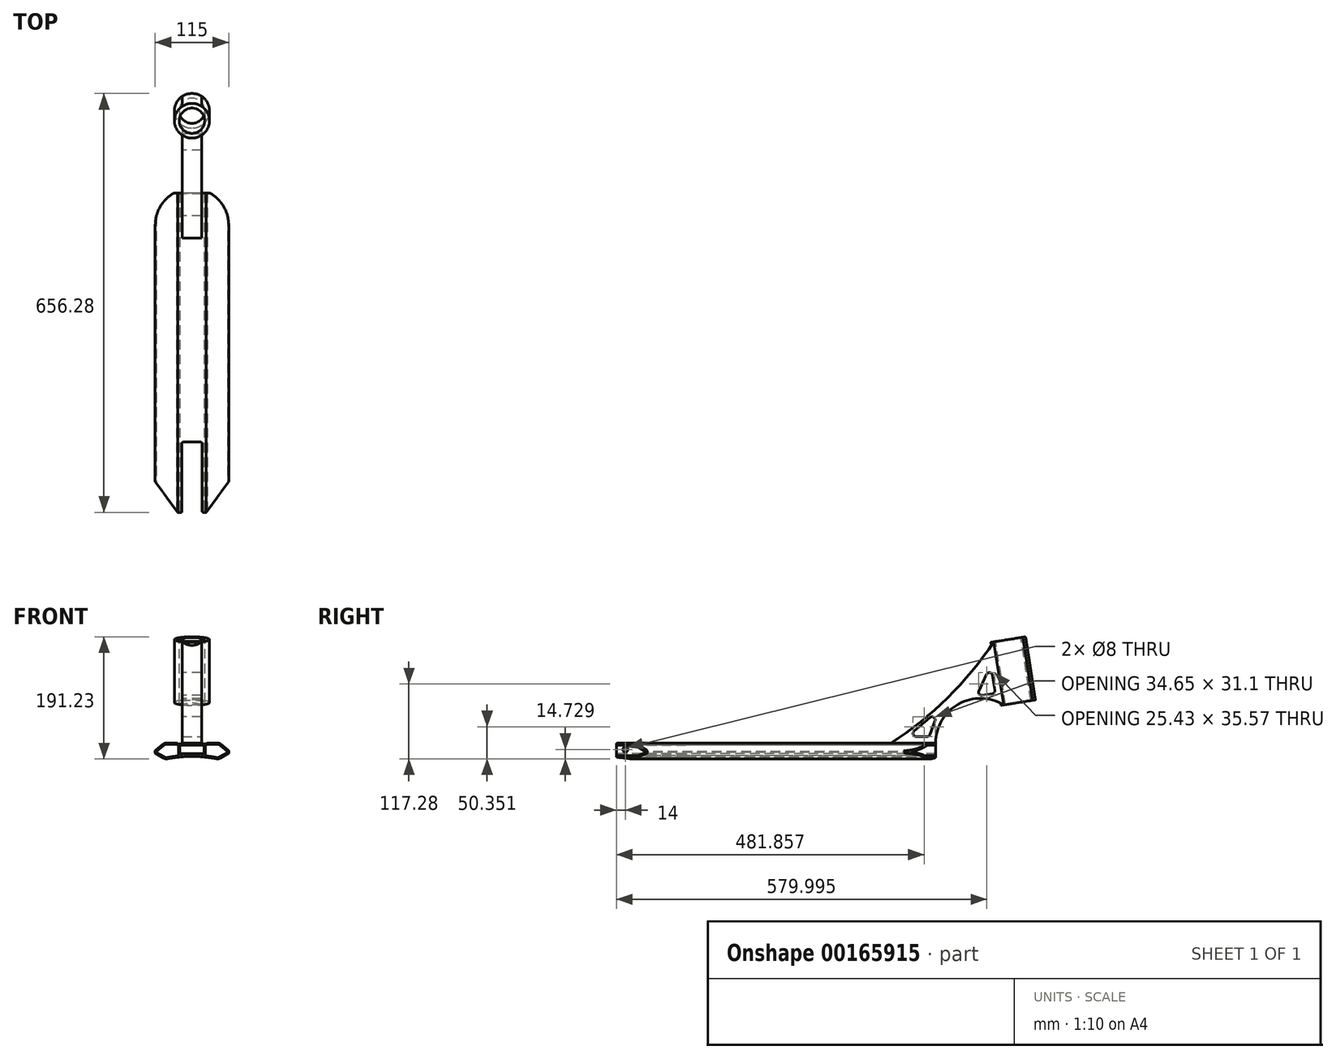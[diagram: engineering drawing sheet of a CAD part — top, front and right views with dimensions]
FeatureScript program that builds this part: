
annotation { "Feature Type Name" : "Feature", "Feature Type Description" : "" }
export const myFeature = defineFeature(function(context is Context, id is Id, definition is map)
    precondition{}
    {
        {
            var Q0;
            Q0=qCreatedBy(makeId("Front.planeOp"),FACE);
            var sketch = newSketch(context, id + "F0", { "sketchPlane" : qUnion([Q0])});
            skLineSegment(sketch, "E0", {"start": v(0, 45.15) * mm, "end": v(0, 0) * mm, "construction": true});
            skLineSegment(sketch, "E1", {"start": v(0, 10.68) * mm, "end": v(22.5, 10.68) * mm});
            skLineSegment(sketch, "E2", {"start": v(22.5, 10.68) * mm, "end": v(22.5, 11.98) * mm});
            skLineSegment(sketch, "E3", {"start": v(22.5, 11.98) * mm, "end": v(43.22, 11.98) * mm});
            skLineSegment(sketch, "E4", {"start": v(43.22, 11.98) * mm, "end": v(57.5, 0) * mm});
            skLineSegment(sketch, "E5", {"start": v(57.5, 0) * mm, "end": v(57.5, -4) * mm});
            skLineSegment(sketch, "E6", {"start": v(57.5, -4) * mm, "end": v(41.36, -13.32) * mm});
            skLineSegment(sketch, "E7.MirrorCS", {"start": v(0, 10.68) * mm, "end": v(-22.5, 10.68) * mm});
            skLineSegment(sketch, "E8.MirrorCS", {"start": v(-22.5, 10.68) * mm, "end": v(-22.5, 11.98) * mm});
            skLineSegment(sketch, "E9.MirrorCS", {"start": v(-22.5, 11.98) * mm, "end": v(-43.22, 11.98) * mm});
            skLineSegment(sketch, "E10.MirrorCS", {"start": v(-43.22, 11.98) * mm, "end": v(-57.5, 0) * mm});
            skLineSegment(sketch, "E11.MirrorCS", {"start": v(-57.5, 0) * mm, "end": v(-57.5, -4) * mm});
            skLineSegment(sketch, "E12.MirrorCS", {"start": v(-57.5, -4) * mm, "end": v(-41.36, -13.32) * mm});
            skArc(sketch, "E13", {"start": v(41.36, -13.32) * mm, "mid": v(0, -9) * mm, "end": v(-41.36, -13.32) * mm});
            skSolve(sketch);
        }
        {
            var Q0;
            Q0 = qSketchRegion(id + "F0", true);
            extrude(context, id + "F1", {"entities" : qUnion([Q0]), "endBound" : BoundingType.SYMMETRIC, "depth" : 500 * mm});
        }
        {
            var Q0;
            Q0=makeQuery(id+"F1.opExtrude","CAP_FACE",FACE,{"disambiguationData":[OSD([sQuery(id+"F0.wireOp",EDGE,"E1"),sQuery(id+"F0.wireOp",EDGE,"E2"),sQuery(id+"F0.wireOp",EDGE,"E3"),sQuery(id+"F0.wireOp",EDGE,"E4"),sQuery(id+"F0.wireOp",EDGE,"E5"),sQuery(id+"F0.wireOp",EDGE,"E6"),sQuery(id+"F0.wireOp",EDGE,"E7.MirrorCS"),sQuery(id+"F0.wireOp",EDGE,"E8.MirrorCS"),sQuery(id+"F0.wireOp",EDGE,"E9.MirrorCS"),sQuery(id+"F0.wireOp",EDGE,"E10.MirrorCS"),sQuery(id+"F0.wireOp",EDGE,"E11.MirrorCS"),sQuery(id+"F0.wireOp",EDGE,"E12.MirrorCS"),sQuery(id+"F0.wireOp",EDGE,"E13")])],"isStart":false});
            var sketch = newSketch(context, id + "F2", { "sketchPlane" : qUnion([Q0])});
            skPoint(sketch, "E14.firstSnap0", {"position": v(-50.36, 8.68) * mm});
            skLineSegment(sketch, "E14.top", {"start": v(-19, -4.32) * mm, "end": v(19, -4.32) * mm});
            skLineSegment(sketch, "E14.left", {"start": v(-19, 8.68) * mm, "end": v(-19, -4.32) * mm});
            skLineSegment(sketch, "E14.right", {"start": v(19, 8.68) * mm, "end": v(19, -4.32) * mm});
            skLineSegment(sketch, "E15", {"start": v(-19, 8.68) * mm, "end": v(19, 8.68) * mm});
            skSolve(sketch);
        }
        {
            var Q0;
            Q0 = qSketchRegion(id + "F2", true);
            extrude(context, id + "F3", {"entities" : qUnion([Q0]), "operationType" : NewBodyOperationType.REMOVE, "endBound" : BoundingType.THROUGH_ALL, "oppositeDirection" : true, "depth" : 500 * mm});
        }
        {
            var Q0;
            Q0=makeQuery(id+"F1.opExtrude","SWEPT_EDGE",EDGE,{"disambiguationData":[OSD([sQuery(id+"F0.wireOp",EDGE,"E8.MirrorCS"),sQuery(id+"F0.wireOp",EDGE,"E9.MirrorCS")])]});
            var Q1;
            Q1=makeQuery(id+"F1.opExtrude","SWEPT_EDGE",EDGE,{"disambiguationData":[OSD([sQuery(id+"F0.wireOp",EDGE,"E2"),sQuery(id+"F0.wireOp",EDGE,"E3")])]});
            fillet(context, id + "F4", {"entities" : qUnion([Q0, Q1]), "radius" : 2 * mm, "tangentPropagation" : true, "allowEdgeOverflow" : false});
        }
        {
            var Q0;
            Q0=makeQuery(id+"F1.opExtrude","SWEPT_EDGE",EDGE,{"disambiguationData":[OSD([sQuery(id+"F0.wireOp",EDGE,"E12.MirrorCS"),sQuery(id+"F0.wireOp",EDGE,"E13")])]});
            var Q1;
            Q1=makeQuery(id+"F1.opExtrude","SWEPT_EDGE",EDGE,{"disambiguationData":[OSD([sQuery(id+"F0.wireOp",EDGE,"E6"),sQuery(id+"F0.wireOp",EDGE,"E13")])]});
            var Q2;
            Q2=makeQuery(id+"F1.opExtrude","SWEPT_EDGE",EDGE,{"disambiguationData":[OSD([sQuery(id+"F0.wireOp",EDGE,"E9.MirrorCS"),sQuery(id+"F0.wireOp",EDGE,"E10.MirrorCS")])]});
            var Q3;
            Q3=makeQuery(id+"F1.opExtrude","SWEPT_EDGE",EDGE,{"disambiguationData":[OSD([sQuery(id+"F0.wireOp",EDGE,"E3"),sQuery(id+"F0.wireOp",EDGE,"E4")])]});
            fillet(context, id + "F5", {"entities" : qUnion([Q0, Q1, Q2, Q3]), "radius" : 9 * mm, "tangentPropagation" : true, "allowEdgeOverflow" : false});
        }
        {
            var Q0;
            Q0=makeQuery(id+"F1.opExtrude","SWEPT_EDGE",EDGE,{"disambiguationData":[OSD([sQuery(id+"F0.wireOp",EDGE,"E4"),sQuery(id+"F0.wireOp",EDGE,"E5")])]});
            var Q1;
            Q1=makeQuery(id+"F1.opExtrude","SWEPT_EDGE",EDGE,{"disambiguationData":[OSD([sQuery(id+"F0.wireOp",EDGE,"E5"),sQuery(id+"F0.wireOp",EDGE,"E6")])]});
            var Q2;
            Q2=makeQuery(id+"F1.opExtrude","SWEPT_EDGE",EDGE,{"disambiguationData":[OSD([sQuery(id+"F0.wireOp",EDGE,"E10.MirrorCS"),sQuery(id+"F0.wireOp",EDGE,"E11.MirrorCS")])]});
            var Q3;
            Q3=makeQuery(id+"F1.opExtrude","SWEPT_EDGE",EDGE,{"disambiguationData":[OSD([sQuery(id+"F0.wireOp",EDGE,"E11.MirrorCS"),sQuery(id+"F0.wireOp",EDGE,"E12.MirrorCS")])]});
            fillet(context, id + "F6", {"entities" : qUnion([Q0, Q1, Q2, Q3]), "radius" : 1 * mm, "tangentPropagation" : true, "allowEdgeOverflow" : false});
        }
        {
            var Q0;
            Q0=makeQuery(id+"F1.opExtrude","CAP_FACE",FACE,{"disambiguationData":[OSD([sQuery(id+"F0.wireOp",EDGE,"E1"),sQuery(id+"F0.wireOp",EDGE,"E2"),sQuery(id+"F0.wireOp",EDGE,"E3"),sQuery(id+"F0.wireOp",EDGE,"E4"),sQuery(id+"F0.wireOp",EDGE,"E5"),sQuery(id+"F0.wireOp",EDGE,"E6"),sQuery(id+"F0.wireOp",EDGE,"E7.MirrorCS"),sQuery(id+"F0.wireOp",EDGE,"E8.MirrorCS"),sQuery(id+"F0.wireOp",EDGE,"E9.MirrorCS"),sQuery(id+"F0.wireOp",EDGE,"E10.MirrorCS"),sQuery(id+"F0.wireOp",EDGE,"E11.MirrorCS"),sQuery(id+"F0.wireOp",EDGE,"E12.MirrorCS"),sQuery(id+"F0.wireOp",EDGE,"E13")])],"isStart":false});
            var sketch = newSketch(context, id + "F7", { "sketchPlane" : qUnion([Q0])});
            skLineSegment(sketch, "E16.0", {"start": v(-22.5, 10.68) * mm, "end": v(-21, 10.68) * mm});
            skPoint(sketch, "E17.0", {"position": v(-23.23, 11.62) * mm});
            skLineSegment(sketch, "E18.0", {"start": v(-24.37, 11.98) * mm, "end": v(-39.95, 11.98) * mm});
            skArc(sketch, "E19.0", {"start": v(-39.95, 11.98) * mm, "mid": v(-43.02, 11.44) * mm, "end": v(-45.73, 9.88) * mm});
            skLineSegment(sketch, "E20.0", {"start": v(-45.73, 9.88) * mm, "end": v(-57.14, 0.3) * mm});
            skPoint(sketch, "E21.0", {"position": v(-57.4, -0.04) * mm});
            skPoint(sketch, "E22.0", {"position": v(-57.5, -1.94) * mm});
            skPoint(sketch, "E23.0", {"position": v(-57, -4.29) * mm});
            skLineSegment(sketch, "E24.0", {"start": v(-57, -4.29) * mm, "end": v(-44.3, -11.62) * mm});
            skArc(sketch, "E25.0", {"start": v(-44.3, -11.62) * mm, "mid": v(-41.3, -12.7) * mm, "end": v(-38.1, -12.66) * mm});
            skArc(sketch, "E26.0", {"start": v(-21, -10.1) * mm, "mid": v(-29.57, -11.2) * mm, "end": v(-38.1, -12.66) * mm});
            skLineSegment(sketch, "E27", {"start": v(-21, 8.68) * mm, "end": v(-21, -8.1) * mm});
            skLineSegment(sketch, "E28.0", {"start": v(-44.45, 8.34) * mm, "end": v(-55.86, -1.23) * mm});
            skArc(sketch, "E28.1", {"start": v(-39.95, 9.98) * mm, "mid": v(-42.34, 9.56) * mm, "end": v(-44.45, 8.34) * mm});
            skLineSegment(sketch, "E29.0", {"start": v(-24.37, 9.98) * mm, "end": v(-39.95, 9.98) * mm});
            skLineSegment(sketch, "E30.0", {"start": v(-22.5, 8.68) * mm, "end": v(-21, 8.68) * mm});
            skFitSpline(sketch, "E31", {"points": [v(-24.37, 9.98) * mm, v(-22.5, 8.68) * mm], "startDerivative": vector(1.87, -1.3) * mm, "endDerivative": vector(1.87, -1.3) * mm});
            skFitSpline(sketch, "E32", {"points": [v(-23.12, 9.11) * mm, v(-23.48, 9.36) * mm], "startDerivative": vector(-0.35, 0.24) * mm, "endDerivative": vector(-0.35, 0.24) * mm});
            skLineSegment(sketch, "E33.0", {"start": v(-56, -2.56) * mm, "end": v(-43.3, -9.88) * mm});
            skArc(sketch, "E33.1", {"start": v(-43.3, -9.88) * mm, "mid": v(-40.96, -10.73) * mm, "end": v(-38.47, -10.7) * mm});
            skArc(sketch, "E33.2", {"start": v(-21, -8.1) * mm, "mid": v(-29.77, -9.2) * mm, "end": v(-38.47, -10.7) * mm});
            skLineSegment(sketch, "E34", {"start": v(-55.86, -1.23) * mm, "end": v(-56, -2.56) * mm});
            skLineSegment(sketch, "E35.MirrorCS", {"start": v(21, 8.68) * mm, "end": v(21, -8.1) * mm});
            skArc(sketch, "E36.MirrorCS", {"start": v(21, -8.1) * mm, "mid": v(29.77, -9.2) * mm, "end": v(38.47, -10.7) * mm});
            skArc(sketch, "E37.MirrorCS", {"start": v(43.3, -9.88) * mm, "mid": v(40.96, -10.73) * mm, "end": v(38.47, -10.7) * mm});
            skLineSegment(sketch, "E38.MirrorCS", {"start": v(56, -2.56) * mm, "end": v(43.3, -9.88) * mm});
            skLineSegment(sketch, "E39.MirrorCS", {"start": v(55.86, -1.23) * mm, "end": v(56, -2.56) * mm});
            skLineSegment(sketch, "E40.MirrorCS", {"start": v(44.45, 8.34) * mm, "end": v(55.86, -1.23) * mm});
            skArc(sketch, "E41.MirrorCS", {"start": v(39.95, 9.98) * mm, "mid": v(42.34, 9.56) * mm, "end": v(44.45, 8.34) * mm});
            skLineSegment(sketch, "E42.MirrorCS", {"start": v(24.37, 9.98) * mm, "end": v(39.95, 9.98) * mm});
            skLineSegment(sketch, "E43.MirrorCS", {"start": v(22.5, 8.68) * mm, "end": v(21, 8.68) * mm});
            skLineSegment(sketch, "E44", {"start": v(24.37, 9.98) * mm, "end": v(22.5, 8.68) * mm});
            skSolve(sketch);
        }
        {
            var Q0;
            Q0 = qSketchRegion(id + "F7", true);
            extrude(context, id + "F8", {"entities" : qUnion([Q0]), "operationType" : NewBodyOperationType.REMOVE, "endBound" : BoundingType.THROUGH_ALL, "oppositeDirection" : true, "depth" : 25 * mm});
        }
        {
            var Q0;
            Q0 = qSketchRegion(id + "F7", true);
            extrude(context, id + "F9", {"entities" : qUnion([Q0]), "operationType" : NewBodyOperationType.REMOVE, "endBound" : BoundingType.THROUGH_ALL, "oppositeDirection" : true, "depth" : 25 * mm});
        }
        {
            var Q0;
            Q0=makeQuery(id+"F1.opExtrude","SWEPT_FACE",FACE,{"disambiguationData":[OSD([sQuery(id+"F0.wireOp",EDGE,"E1"),sQuery(id+"F0.wireOp",EDGE,"E7.MirrorCS")])]});
            var sketch = newSketch(context, id + "F10", { "sketchPlane" : qUnion([Q0])});
            skArc(sketch, "E45", {"start": v(57.5, 200) * mm, "mid": v(0, 257.5) * mm, "end": v(-57.5, 200) * mm});
            skLineSegment(sketch, "E46", {"start": v(-57.5, 280) * mm, "end": v(57.5, 280) * mm});
            skLineSegment(sketch, "E47", {"start": v(57.5, 200) * mm, "end": v(57.5, 280) * mm});
            skPoint(sketch, "E48.orphan", {"position": v(63.8, 280) * mm});
            skLineSegment(sketch, "E49", {"start": v(-57.5, 200) * mm, "end": v(-57.5, 280) * mm});
            skPoint(sketch, "E50.orphan", {"position": v(-57.5, 278.01) * mm});
            skSolve(sketch);
        }
        {
            var Q0;
            Q0 = qSketchRegion(id + "F10", true);
            extrude(context, id + "F11", {"entities" : qUnion([Q0]), "operationType" : NewBodyOperationType.REMOVE, "endBound" : BoundingType.SYMMETRIC, "oppositeDirection" : true, "depth" : 100 * mm});
        }
        {
            var Q0;
            Q0=makeQuery(id+"F1.opExtrude","SWEPT_FACE",FACE,{"disambiguationData":[OSD([sQuery(id+"F0.wireOp",EDGE,"E9.MirrorCS")])]});
            var sketch = newSketch(context, id + "F12", { "sketchPlane" : qUnion([Q0])});
            skLineSegment(sketch, "E51", {"start": v(-68, -187.37) * mm, "end": v(-22.5, -250) * mm});
            skLineSegment(sketch, "E52", {"start": v(-22.5, -250) * mm, "end": v(-16, -250) * mm});
            skLineSegment(sketch, "E53", {"start": v(-16, -250) * mm, "end": v(-16, -140) * mm});
            skLineSegment(sketch, "E54", {"start": v(-16, -140) * mm, "end": v(16, -140) * mm});
            skLineSegment(sketch, "E55", {"start": v(16, -140) * mm, "end": v(16, -250) * mm});
            skLineSegment(sketch, "E56", {"start": v(16, -250) * mm, "end": v(22.5, -250) * mm});
            skLineSegment(sketch, "E57", {"start": v(22.5, -250) * mm, "end": v(68, -187.37) * mm});
            skLineSegment(sketch, "E58", {"start": v(68, -187.37) * mm, "end": v(68, -287.37) * mm});
            skLineSegment(sketch, "E59", {"start": v(68, -287.37) * mm, "end": v(-68, -287.37) * mm});
            skLineSegment(sketch, "E60", {"start": v(-68, -287.37) * mm, "end": v(-68, -187.37) * mm});
            skSolve(sketch);
        }
        {
            var Q0;
            Q0 = qSketchRegion(id + "F12", true);
            extrude(context, id + "F13", {"entities" : qUnion([Q0]), "operationType" : NewBodyOperationType.REMOVE, "endBound" : BoundingType.THROUGH_ALL, "oppositeDirection" : true, "depth" : 25 * mm});
        }
        {
            var Q0;
            {var subQ2=sQuery(id+"F12.wireOp",EDGE,"E53");Q0=makeQuery(id+"F13.boolean.opBoolean","COPY",EDGE,{"disambiguationData":[TD([makeQuery(id+"F3.boolean.opBoolean","COPY",FACE,{"derivedFrom":makeQuery(id+"F3.opExtrude","SWEPT_FACE",FACE,{"disambiguationData":[OSD([sQuery(id+"F2.wireOp",EDGE,"E15")])]})})])],"derivedFrom":makeQuery(id+"F13.opExtrude","SWEPT_EDGE",EDGE,{"disambiguationData":[OSD([sQuery(id+"F12.wireOp",EDGE,"E52"),subQ2])]})});}
            var Q1;
            {var subQ0=sQuery(id+"F0.wireOp",EDGE,"E13");var subQ1=sQuery(id+"F12.wireOp",EDGE,"E53");Q1=makeQuery(id+"F13.boolean.opBoolean","COPY",EDGE,{"disambiguationData":[TD([makeQuery(id+"F1.opExtrude","SWEPT_FACE",FACE,{"disambiguationData":[OSD([subQ0])]})])],"derivedFrom":makeQuery(id+"F13.opExtrude","SWEPT_EDGE",EDGE,{"disambiguationData":[OSD([sQuery(id+"F12.wireOp",EDGE,"E52"),subQ1])]})});}
            var Q2;
            {var subQ0=sQuery(id+"F12.wireOp",EDGE,"E54");var subQ1=sQuery(id+"F12.wireOp",EDGE,"E53");Q2=makeQuery(id+"F13.boolean.opBoolean","COPY",EDGE,{"disambiguationData":[TD([makeQuery(id+"F1.opExtrude","SWEPT_FACE",FACE,{"disambiguationData":[OSD([sQuery(id+"F0.wireOp",EDGE,"E13")])]})])],"derivedFrom":makeQuery(id+"F13.opExtrude","SWEPT_EDGE",EDGE,{"disambiguationData":[OSD([subQ1,subQ0])]})});}
            var Q3;
            {var subQ0=sQuery(id+"F12.wireOp",EDGE,"E53");var subQ1=sQuery(id+"F12.wireOp",EDGE,"E54");Q3=makeQuery(id+"F13.boolean.opBoolean","COPY",EDGE,{"disambiguationData":[TD([makeQuery(id+"F3.boolean.opBoolean","COPY",FACE,{"derivedFrom":makeQuery(id+"F3.opExtrude","SWEPT_FACE",FACE,{"disambiguationData":[OSD([sQuery(id+"F2.wireOp",EDGE,"E15")])]})})])],"derivedFrom":makeQuery(id+"F13.opExtrude","SWEPT_EDGE",EDGE,{"disambiguationData":[OSD([subQ0,subQ1])]})});}
            var Q4;
            {var subQ0=sQuery(id+"F0.wireOp",EDGE,"E13");var subQ1=sQuery(id+"F12.wireOp",EDGE,"E55");Q4=makeQuery(id+"F13.boolean.opBoolean","COPY",EDGE,{"disambiguationData":[TD([makeQuery(id+"F1.opExtrude","SWEPT_FACE",FACE,{"disambiguationData":[OSD([subQ0])]})])],"derivedFrom":makeQuery(id+"F13.opExtrude","SWEPT_EDGE",EDGE,{"disambiguationData":[OSD([subQ1,sQuery(id+"F12.wireOp",EDGE,"E56")])]})});}
            var Q5;
            {var subQ2=sQuery(id+"F12.wireOp",EDGE,"E55");Q5=makeQuery(id+"F13.boolean.opBoolean","COPY",EDGE,{"disambiguationData":[TD([makeQuery(id+"F3.boolean.opBoolean","COPY",FACE,{"derivedFrom":makeQuery(id+"F3.opExtrude","SWEPT_FACE",FACE,{"disambiguationData":[OSD([sQuery(id+"F2.wireOp",EDGE,"E15")])]})})])],"derivedFrom":makeQuery(id+"F13.opExtrude","SWEPT_EDGE",EDGE,{"disambiguationData":[OSD([subQ2,sQuery(id+"F12.wireOp",EDGE,"E56")])]})});}
            var Q6;
            {var subQ0=sQuery(id+"F12.wireOp",EDGE,"E54");var subQ1=sQuery(id+"F12.wireOp",EDGE,"E55");Q6=makeQuery(id+"F13.boolean.opBoolean","COPY",EDGE,{"disambiguationData":[TD([makeQuery(id+"F1.opExtrude","SWEPT_FACE",FACE,{"disambiguationData":[OSD([sQuery(id+"F0.wireOp",EDGE,"E13")])]})])],"derivedFrom":makeQuery(id+"F13.opExtrude","SWEPT_EDGE",EDGE,{"disambiguationData":[OSD([subQ0,subQ1])]})});}
            var Q7;
            {var subQ0=sQuery(id+"F12.wireOp",EDGE,"E54");var subQ1=sQuery(id+"F12.wireOp",EDGE,"E55");Q7=makeQuery(id+"F13.boolean.opBoolean","COPY",EDGE,{"disambiguationData":[TD([makeQuery(id+"F3.boolean.opBoolean","COPY",FACE,{"derivedFrom":makeQuery(id+"F3.opExtrude","SWEPT_FACE",FACE,{"disambiguationData":[OSD([sQuery(id+"F2.wireOp",EDGE,"E15")])]})})])],"derivedFrom":makeQuery(id+"F13.opExtrude","SWEPT_EDGE",EDGE,{"disambiguationData":[OSD([subQ0,subQ1])]})});}
            fillet(context, id + "F14", {"entities" : qUnion([Q0, Q1, Q2, Q3, Q4, Q5, Q6, Q7]), "radius" : 2 * mm, "tangentPropagation" : true, "allowEdgeOverflow" : false});
        }
        {
            var Q0;
            Q0=qCreatedBy(makeId("Right.planeOp"),FACE);
            var sketch = newSketch(context, id + "F15", { "sketchPlane" : qUnion([Q0])});
            skLineSegment(sketch, "E61", {"start": v(180, 11.98) * mm, "end": v(250, 11.98) * mm});
            skArc(sketch, "E62", {"start": v(356.44, 71.75) * mm, "mid": v(285.73, 73.02) * mm, "end": v(250, 11.98) * mm});
            skLineSegment(sketch, "E63", {"start": v(356.44, 71.75) * mm, "end": v(401.87, 78.94) * mm});
            skLineSegment(sketch, "E64", {"start": v(401.87, 78.94) * mm, "end": v(386.23, 177.71) * mm});
            skLineSegment(sketch, "E65", {"start": v(386.23, 177.71) * mm, "end": v(340.8, 170.52) * mm});
            skArc(sketch, "E66", {"start": v(180, 11.98) * mm, "mid": v(268.62, 82.9) * mm, "end": v(340.8, 170.52) * mm});
            skSolve(sketch);
        }
        {
            var Q0;
            Q0 = qSketchRegion(id + "F15", true);
            extrude(context, id + "F16", {"entities" : qUnion([Q0]), "operationType" : NewBodyOperationType.ADD, "endBound" : BoundingType.SYMMETRIC, "depth" : 30 * mm});
        }
        {
            var Q0;
            Q0=makeQuery(id+"F16.opExtrude","SWEPT_FACE",FACE,{"disambiguationData":[OSD([sQuery(id+"F15.wireOp",EDGE,"E65")])]});
            var sketch = newSketch(context, id + "F17", { "sketchPlane" : qUnion([Q0])});
            skCircle(sketch, "E67", {"center": v(0, 386.28) * mm, "radius": 27.46 * mm});
            skSolve(sketch);
        }
        {
            var Q0;
            Q0 = qSketchRegion(id + "F17", true);
            var Q1;
            Q1=makeQuery(id+"F16.opExtrude","SWEPT_FACE",FACE,{"disambiguationData":[OSD([sQuery(id+"F15.wireOp",EDGE,"E63")])]});
            var Q2;
            Q2=makeQuery(id+"F16.opExtrude","SWEPT_BODY",BODY,{"disambiguationData":[OSD([sQuery(id+"F15.wireOp",EDGE,"E61"),sQuery(id+"F15.wireOp",EDGE,"E62"),sQuery(id+"F15.wireOp",EDGE,"E63"),sQuery(id+"F15.wireOp",EDGE,"E64"),sQuery(id+"F15.wireOp",EDGE,"E65"),sQuery(id+"F15.wireOp",EDGE,"E66")])]});
            extrude(context, id + "F18", {"entities" : qUnion([Q0]), "operationType" : NewBodyOperationType.ADD, "endBound" : BoundingType.UP_TO_SURFACE, "oppositeDirection" : true, "endBoundEntityFace" : qUnion([Q1]), "endBoundEntityBody" : qUnion([Q2]), "depth" : 25 * mm});
        }
        {
            var Q0;
            Q0=makeQuery(id+"F18.boolean.opBoolean","MERGE",FACE,{"derivedFrom":[makeQuery(id+"F16.opExtrude","SWEPT_FACE",FACE,{"disambiguationData":[OSD([sQuery(id+"F15.wireOp",EDGE,"E65")])]}),makeQuery(id+"F18.opExtrude","CAP_FACE",FACE,{"disambiguationData":[OSD([sQuery(id+"F17.wireOp",EDGE,"E67")])],"isStart":true})]});
            var sketch = newSketch(context, id + "F19", { "sketchPlane" : qUnion([Q0])});
            skPoint(sketch, "E68", {"position": v(0, 386.28) * mm});
            skSolve(sketch);
        }
        {
            var Q0;
            Q0=sQuery(id+"F19.wireOp",VERTEX,"E68");
            var Q1;
            Q1=makeQuery(id+"F16.opExtrude","SWEPT_BODY",BODY,{"disambiguationData":[OSD([sQuery(id+"F15.wireOp",EDGE,"E61"),sQuery(id+"F15.wireOp",EDGE,"E62"),sQuery(id+"F15.wireOp",EDGE,"E63"),sQuery(id+"F15.wireOp",EDGE,"E64"),sQuery(id+"F15.wireOp",EDGE,"E65"),sQuery(id+"F15.wireOp",EDGE,"E66")])]});
            hole(context, id + "F20", {"style" : HoleStyle.SIMPLE, "endStyle" : HoleEndStyle.THROUGH, "holeDiameter" : 40 * mm, "locations" : qUnion([Q0]), "scope" : qUnion([Q1]), "isTappedThrough" : true});
        }
        {
            var Q0;
            Q0=makeQuery(id+"F8.boolean.opBoolean","COPY",FACE,{"derivedFrom":makeQuery(id+"F8.opExtrude","SWEPT_FACE",FACE,{"disambiguationData":[OSD([sQuery(id+"F7.wireOp",EDGE,"E35.MirrorCS")])]})});
            var sketch = newSketch(context, id + "F21", { "sketchPlane" : qUnion([Q0])});
            skPoint(sketch, "E69", {"position": v(-236, 1.9) * mm});
            skSolve(sketch);
        }
        {
            var Q0;
            Q0=sQuery(id+"F21.wireOp",VERTEX,"E69");
            var Q1;
            Q1=makeQuery(id+"F1.opExtrude","SWEPT_BODY",BODY,{"disambiguationData":[OSD([sQuery(id+"F0.wireOp",EDGE,"E1"),sQuery(id+"F0.wireOp",EDGE,"E2"),sQuery(id+"F0.wireOp",EDGE,"E3"),sQuery(id+"F0.wireOp",EDGE,"E4"),sQuery(id+"F0.wireOp",EDGE,"E5"),sQuery(id+"F0.wireOp",EDGE,"E6"),sQuery(id+"F0.wireOp",EDGE,"E7.MirrorCS"),sQuery(id+"F0.wireOp",EDGE,"E8.MirrorCS"),sQuery(id+"F0.wireOp",EDGE,"E9.MirrorCS"),sQuery(id+"F0.wireOp",EDGE,"E10.MirrorCS"),sQuery(id+"F0.wireOp",EDGE,"E11.MirrorCS"),sQuery(id+"F0.wireOp",EDGE,"E12.MirrorCS"),sQuery(id+"F0.wireOp",EDGE,"E13")])]});
            hole(context, id + "F22", {"style" : HoleStyle.SIMPLE, "endStyle" : HoleEndStyle.THROUGH, "holeDiameter" : 8 * mm, "locations" : qUnion([Q0]), "scope" : qUnion([Q1]), "isTappedThrough" : true});
        }
        {
            var Q0;
            Q0=makeQuery(id+"F1.opExtrude","SWEPT_FACE",FACE,{"disambiguationData":[OSD([sQuery(id+"F0.wireOp",EDGE,"E5")])]});
            var sketch = newSketch(context, id + "F23", { "sketchPlane" : qUnion([Q0])});
            skLineSegment(sketch, "E70", {"start": v(206, 21.98) * mm, "end": v(240, 21.98) * mm});
            skLineSegment(sketch, "E71", {"start": v(240, 21.98) * mm, "end": v(255.4, 64.27) * mm});
            skLineSegment(sketch, "E72", {"start": v(255.4, 64.27) * mm, "end": v(206, 21.98) * mm});
            skLineSegment(sketch, "E73", {"start": v(336.4, 134.38) * mm, "end": v(313.8, 85.24) * mm});
            skLineSegment(sketch, "E74", {"start": v(313.8, 85.24) * mm, "end": v(343.43, 89.94) * mm});
            skLineSegment(sketch, "E75", {"start": v(343.43, 89.94) * mm, "end": v(336.4, 134.38) * mm});
            skSolve(sketch);
        }
        {
            var Q0;
            Q0 = qSketchRegion(id + "F23", true);
            extrude(context, id + "F24", {"entities" : qUnion([Q0]), "operationType" : NewBodyOperationType.REMOVE, "endBound" : BoundingType.THROUGH_ALL, "oppositeDirection" : true, "depth" : 25 * mm});
        }
        {
            var Q0;
            Q0=makeQuery(id+"F24.boolean.opBoolean","COPY",EDGE,{"derivedFrom":makeQuery(id+"F24.opExtrude","SWEPT_EDGE",EDGE,{"disambiguationData":[OSD([sQuery(id+"F23.wireOp",EDGE,"E74"),sQuery(id+"F23.wireOp",EDGE,"E75")])]})});
            var Q1;
            Q1=makeQuery(id+"F24.boolean.opBoolean","COPY",EDGE,{"derivedFrom":makeQuery(id+"F24.opExtrude","SWEPT_EDGE",EDGE,{"disambiguationData":[OSD([sQuery(id+"F23.wireOp",EDGE,"E70"),sQuery(id+"F23.wireOp",EDGE,"E71")])]})});
            var Q2;
            Q2=makeQuery(id+"F24.boolean.opBoolean","COPY",EDGE,{"derivedFrom":makeQuery(id+"F24.opExtrude","SWEPT_EDGE",EDGE,{"disambiguationData":[OSD([sQuery(id+"F23.wireOp",EDGE,"E71"),sQuery(id+"F23.wireOp",EDGE,"E72")])]})});
            var Q3;
            Q3=makeQuery(id+"F24.boolean.opBoolean","COPY",EDGE,{"derivedFrom":makeQuery(id+"F24.opExtrude","SWEPT_EDGE",EDGE,{"disambiguationData":[OSD([sQuery(id+"F23.wireOp",EDGE,"E73"),sQuery(id+"F23.wireOp",EDGE,"E75")])]})});
            var Q4;
            Q4=makeQuery(id+"F24.boolean.opBoolean","COPY",EDGE,{"derivedFrom":makeQuery(id+"F24.opExtrude","SWEPT_EDGE",EDGE,{"disambiguationData":[OSD([sQuery(id+"F23.wireOp",EDGE,"E73"),sQuery(id+"F23.wireOp",EDGE,"E74")])]})});
            var Q5;
            Q5=makeQuery(id+"F24.boolean.opBoolean","COPY",EDGE,{"derivedFrom":makeQuery(id+"F24.opExtrude","SWEPT_EDGE",EDGE,{"disambiguationData":[OSD([sQuery(id+"F23.wireOp",EDGE,"E70"),sQuery(id+"F23.wireOp",EDGE,"E72")])]})});
            fillet(context, id + "F25", {"entities" : qUnion([Q0, Q1, Q2, Q3, Q4, Q5]), "radius" : 5 * mm, "tangentPropagation" : true, "allowEdgeOverflow" : false});
        }
    });
